# Revit family: Haworth_LC2_Ottoman
name_source: partatom
category: Furniture
revit_build: Autodesk Revit 2018 (Build: 20170223_1515(x64)
units: mm (PartAtom-declared; Revit-internal decimal feet)

## family parameters
Always vertical = Yes
Cut with Voids When Loaded = No
OmniClass Number = 23.40.20.00
OmniClass Title = General Furniture and Specialties
Room Calculation Point = No
Shared = No
Work Plane-Based = No

## types (1)
- HCCS-LC2F
    Actual Depth = 1' - 10"
    Actual Height = 1' - 4"
    Actual Width = 2' - 4 1/2"
    Arm Width = 0' - 4 1/4"
    Assembly Code = E2020200
    Description = Haworth LC2 Ottoman
    Edge Offset = 0' - 0 1/4"
    Frame Radius = 0' - 0 3/8"
    Frame Thickness = 0' - 0 3/4"
    Glide Finish = Haworth _ Paint _ Black
    Half Width = 1' - 2 1/4"
    Inside Depth = 1' - 8 1/2"
    Leg Offset = 0' - 4 1/4"
    Manufacturer = Haworth
    Model = HCCS-LC2F
    Revision = 4
    Size = Verify Final Dim. w/ Haworth
    URL = http://www.haworth.com
    URL - Product = http://www.haworth.com
    Warranty = http://www.haworth.com

## geometry (parser evidence)
native form markers: Sweep x2
no freeform markers — native parametric forms only
